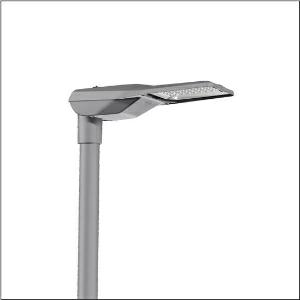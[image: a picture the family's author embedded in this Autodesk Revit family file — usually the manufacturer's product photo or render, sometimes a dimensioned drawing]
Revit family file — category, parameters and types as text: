
# Revit family: streetlight_sl_21_iq_mini___st1_0a_5xe2d31v08jb_ee78
name_source: partatom
category: Lighting Fixtures
units: mm (PartAtom-declared; Revit-internal decimal feet)

## family parameters
Cut with Voids When Loaded = No
Host = Face
Light Source = No
Part Type = Normal
Room Calculation Point = No
Round Connector Dimension = Use Diameter
Shared = No

## types (1)
- --- (1 x LED, 11210 lm, 72.5 W, 3000K)
    Apparent Load = 73 VA
    CIE Flux Codes = 40 73 97 100 100
    Color Rendering = 70
    Color Temperature = 3000K
    Default Elevation = 1800 mm
    Description = Streetlight SL 21 iQ mini, mast luminaire, primary light control with lens, of PMMA, primary optical cover: cover, of toughened safety glass, transparent, light distribution: ST1.0a, light emission: direct distribution, primary light characteristic: asymmetric, installation type: post-top, side-entry, LED, High Power LED, rated luminous flux: 11.210lm, luminous efficacy: 155lm/W, light colour: 730, colour temperature: 3000K, control: presetting dimming logarithmic, Street-Remote, Auto-Match, Temp-Guard, Lumen-Switch, Night-Set, Smart-Wire, Light-Fading, Desk-Remote (wireless, voltage-free reading and setting of iQ features in the workshop via application-optimized NFC function/RFID function), optimised constant luminous flux control (CLO 2.0), mains connection: 220..240V, AC, 50/60Hz, start of lifetime: 73W, end of service life: 76W, reduction: 33W, luminaire housing, of diecast aluminium, powder-coated, Siteco® metallic grey (DB 702S), corrosivity category C5 mid according to DIN EN ISO 12944, please order mast flange separately, inclination adjustable: 0°, 5°, 10°, 15°, sealing non-destructively replaceable, multi-level sealing system, length: 628mm, width: 235mm, height: 110mm, mast flange for spigot size: 42mm (side-entry): 5XC10008XM4, 60/48mm (side-entry/post-top): 5XC10108XM2, 76/60mm (side-entry/post-top): 5XC10108XM1, Smart Interface above, protection rating (complete): IP66, insulation class (complete): insulation class II (safety insulation), certification: CE, ENEC, ENEC+, VDE, impact resistance: IK09, permissible operating ambient temperature for outdoor applications: -40..+50°C, standard-compliant lighting for roads and squares, packaging unit: 1 piece

Light Distribution: ST1.0a
    Height = 110 mm
    Lamp = 1 x LED
    Lamp Light Flux = 11210 lm
    Lamp Power = 72.5 W
    Lamp count = 1
    Length = 625 mm
    Luminous efficacy = 155 lm/W
    Manufacturer = Siteco
    ModVariant = No
    Model = 5XE2D31V08JB
    Number of Poles = 1
    OnlyDefault = Yes
    Power Factor = 1
    Product Name = Streetlight SL 21 iQ mini | ST1.0a
    Product group = mast luminaire | pylon top
    ProductGroupID = 6100
    Protection Class = Protection class II
    Protection Degree = IP 66
    RLX_Detail_Level = 1
    RLX_Emergency_Light_Flux = 0 lm
    RLX_Emergency_Type = 0
    RLX_Emergency_Type_DB = No
    RlxData = <blob elided: 92313 chars, md5=a2cd2eb4>
    Socket = socket
    Standby Power = 0 W
    System Light Flux = 11210 lm
    System Power = 73 W
    Type Comments = factory setting: luminous flux: 100 % | dim-lin: 254 | 755 mA
    Type Image = l_1003515.jpg
    URL = http://relux.com
    VarID = @adj_044225
    Voltage = 0 V
    Weight = 0.00 kg
    Width = 234 mm

## geometry (parser evidence)
native form markers: Blend x4, Sweep x11
no freeform markers — native parametric forms only
